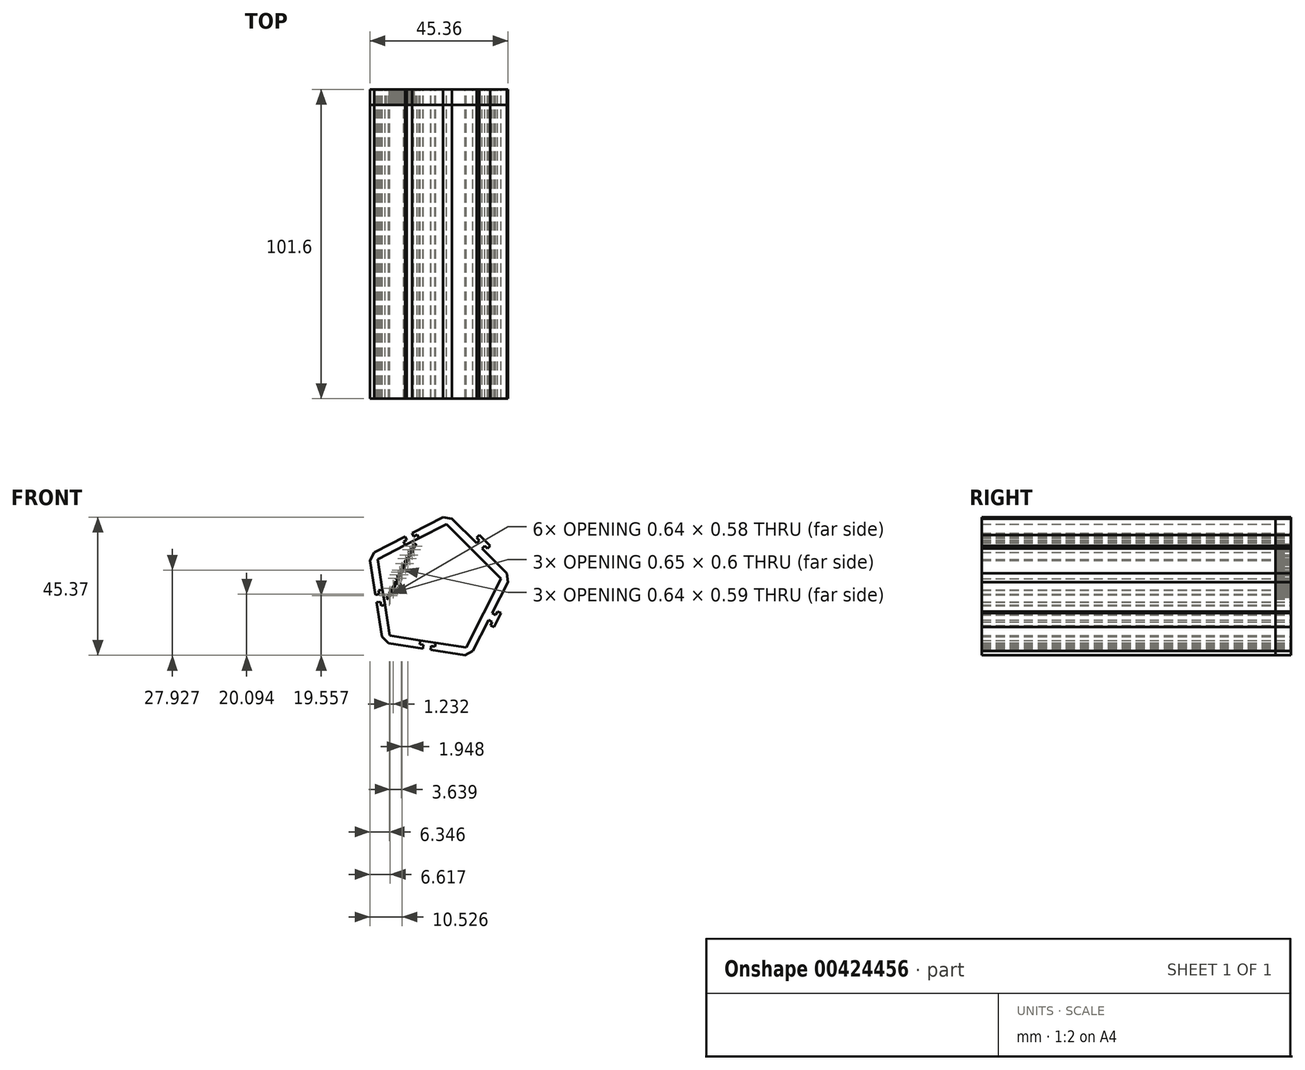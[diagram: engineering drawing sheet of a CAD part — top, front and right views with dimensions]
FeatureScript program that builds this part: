
annotation { "Feature Type Name" : "Feature", "Feature Type Description" : "" }
export const myFeature = defineFeature(function(context is Context, id is Id, definition is map)
    precondition{}
    {
        {
            var Q0;
            Q0=qCreatedBy(makeId("Front.planeOp"),FACE);
            var sketch = newSketch(context, id + "F0", { "sketchPlane" : qUnion([Q0])});
            skLineSegment(sketch, "E0", {"start": v(-27.51, 38.72) * mm, "end": v(-23.54, 13.64) * mm});
            skLineSegment(sketch, "E1", {"start": v(-23.54, 13.64) * mm, "end": v(1.55, 9.66) * mm});
            skLineSegment(sketch, "E2", {"start": v(1.55, 9.66) * mm, "end": v(13.08, 32.3) * mm});
            skLineSegment(sketch, "E3", {"start": v(13.08, 32.3) * mm, "end": v(-4.88, 50.26) * mm});
            skLineSegment(sketch, "E4", {"start": v(-4.88, 50.26) * mm, "end": v(-27.51, 38.72) * mm});
            skLineSegment(sketch, "E5", {"start": v(-27.51, 38.72) * mm, "end": v(-28.67, 40.99) * mm});
            skLineSegment(sketch, "E6", {"start": v(-4.88, 50.26) * mm, "end": v(-6.04, 52.52) * mm});
            skLineSegment(sketch, "E7", {"start": v(-28.67, 40.99) * mm, "end": v(-18.48, 46.18) * mm});
            skLineSegment(sketch, "E8", {"start": v(-6.04, 52.52) * mm, "end": v(-16.22, 47.33) * mm});
            skLineSegment(sketch, "E9", {"start": v(-18.48, 46.18) * mm, "end": v(-17.9, 45.04) * mm});
            skLineSegment(sketch, "E10", {"start": v(-17.9, 45.04) * mm, "end": v(-19.04, 44.47) * mm});
            skLineSegment(sketch, "E11", {"start": v(-19.04, 44.47) * mm, "end": v(-18.46, 43.34) * mm});
            skLineSegment(sketch, "E12", {"start": v(-16.22, 47.33) * mm, "end": v(-15.64, 46.2) * mm});
            skLineSegment(sketch, "E13", {"start": v(-15.64, 46.2) * mm, "end": v(-14.51, 46.77) * mm});
            skLineSegment(sketch, "E14", {"start": v(-14.51, 46.77) * mm, "end": v(-13.94, 45.64) * mm});
            skLineSegment(sketch, "E15", {"start": v(-4.88, 50.26) * mm, "end": v(-3.09, 52.05) * mm});
            skLineSegment(sketch, "E16", {"start": v(13.08, 32.3) * mm, "end": v(14.87, 34.1) * mm});
            skLineSegment(sketch, "E17", {"start": v(-3.09, 52.05) * mm, "end": v(5, 43.97) * mm});
            skLineSegment(sketch, "E18", {"start": v(14.87, 34.1) * mm, "end": v(6.8, 42.17) * mm});
            skLineSegment(sketch, "E19", {"start": v(5, 43.97) * mm, "end": v(5.9, 44.87) * mm});
            skLineSegment(sketch, "E20", {"start": v(6.8, 42.17) * mm, "end": v(7.69, 43.07) * mm});
            skLineSegment(sketch, "E21", {"start": v(5.9, 44.87) * mm, "end": v(5, 45.76) * mm});
            skLineSegment(sketch, "E22", {"start": v(5, 45.76) * mm, "end": v(5.9, 46.66) * mm});
            skLineSegment(sketch, "E23", {"start": v(5.9, 46.66) * mm, "end": v(9.49, 43.07) * mm});
            skLineSegment(sketch, "E24", {"start": v(9.49, 43.07) * mm, "end": v(8.59, 42.17) * mm});
            skLineSegment(sketch, "E25", {"start": v(7.69, 43.07) * mm, "end": v(8.59, 42.17) * mm});
            skLineSegment(sketch, "E26", {"start": v(-6.04, 52.52) * mm, "end": v(-3.09, 52.05) * mm});
            skLineSegment(sketch, "E27", {"start": v(13.08, 32.3) * mm, "end": v(15.34, 31.14) * mm});
            skLineSegment(sketch, "E28", {"start": v(15.34, 31.14) * mm, "end": v(10.15, 20.96) * mm});
            skLineSegment(sketch, "E29", {"start": v(1.55, 9.66) * mm, "end": v(3.8, 8.5) * mm});
            skLineSegment(sketch, "E30", {"start": v(3.8, 8.5) * mm, "end": v(9, 18.7) * mm});
            skLineSegment(sketch, "E31", {"start": v(14.87, 34.1) * mm, "end": v(15.34, 31.14) * mm});
            skLineSegment(sketch, "E32", {"start": v(-23.54, 13.64) * mm, "end": v(-23.94, 11.13) * mm});
            skLineSegment(sketch, "E33", {"start": v(-23.94, 11.13) * mm, "end": v(-12.65, 9.34) * mm});
            skLineSegment(sketch, "E34", {"start": v(-12.65, 9.34) * mm, "end": v(-12.45, 10.6) * mm});
            skLineSegment(sketch, "E35", {"start": v(-12.45, 10.6) * mm, "end": v(-13.7, 10.8) * mm});
            skLineSegment(sketch, "E36", {"start": v(-13.7, 10.8) * mm, "end": v(-13.5, 12.05) * mm});
            skLineSegment(sketch, "E37", {"start": v(1.55, 9.66) * mm, "end": v(1.15, 7.15) * mm});
            skLineSegment(sketch, "E38", {"start": v(1.15, 7.15) * mm, "end": v(-10.14, 8.94) * mm});
            skLineSegment(sketch, "E39", {"start": v(-10.14, 8.94) * mm, "end": v(-9.94, 10.2) * mm});
            skLineSegment(sketch, "E40", {"start": v(-9.94, 10.2) * mm, "end": v(-8.69, 10) * mm});
            skLineSegment(sketch, "E41", {"start": v(-8.69, 10) * mm, "end": v(-8.49, 11.25) * mm});
            skLineSegment(sketch, "E42", {"start": v(1.15, 7.15) * mm, "end": v(3.8, 8.5) * mm});
            skLineSegment(sketch, "E43", {"start": v(-27.51, 38.72) * mm, "end": v(-30.02, 38.33) * mm});
            skLineSegment(sketch, "E44", {"start": v(-30.02, 38.33) * mm, "end": v(-28.24, 27.04) * mm});
            skLineSegment(sketch, "E45", {"start": v(-28.24, 27.04) * mm, "end": v(-26.98, 27.24) * mm});
            skLineSegment(sketch, "E46", {"start": v(-26.98, 27.24) * mm, "end": v(-27.18, 28.5) * mm});
            skLineSegment(sketch, "E47", {"start": v(-27.18, 28.5) * mm, "end": v(-25.93, 28.69) * mm});
            skLineSegment(sketch, "E48", {"start": v(-28.67, 40.99) * mm, "end": v(-30.02, 38.33) * mm});
            skLineSegment(sketch, "E49", {"start": v(-23.54, 13.64) * mm, "end": v(-26.05, 13.24) * mm});
            skLineSegment(sketch, "E50", {"start": v(-26.05, 13.24) * mm, "end": v(-23.94, 11.13) * mm});
            skLineSegment(sketch, "E51", {"start": v(-26.05, 13.24) * mm, "end": v(-27.84, 24.53) * mm});
            skLineSegment(sketch, "E52", {"start": v(-27.84, 24.53) * mm, "end": v(-26.58, 24.73) * mm});
            skLineSegment(sketch, "E53", {"start": v(-26.58, 24.73) * mm, "end": v(-26.39, 23.47) * mm});
            skLineSegment(sketch, "E54", {"start": v(-26.39, 23.47) * mm, "end": v(-25.13, 23.67) * mm});
            skLineSegment(sketch, "E55", {"start": v(10.15, 20.96) * mm, "end": v(11.28, 20.38) * mm});
            skLineSegment(sketch, "E56", {"start": v(11.28, 20.38) * mm, "end": v(11.86, 21.51) * mm});
            skLineSegment(sketch, "E57", {"start": v(11.86, 21.51) * mm, "end": v(13, 20.96) * mm});
            skLineSegment(sketch, "E58", {"start": v(10.14, 18.14) * mm, "end": v(9.56, 17) * mm});
            skLineSegment(sketch, "E59", {"start": v(9.56, 17) * mm, "end": v(10.7, 16.43) * mm});
            skLineSegment(sketch, "E60", {"start": v(13, 20.96) * mm, "end": v(10.7, 16.43) * mm});
            skLineSegment(sketch, "E61", {"start": v(9, 18.7) * mm, "end": v(10.14, 18.14) * mm});
            skText(sketch, "E62", { "text": "Designed by Jefferson DeGrove Bishop", "fontName": "Arimo-Regular.ttf"});
            const initialGuessF0  = {"E62": [-0.02392, 0.02554, 0.44713, 0.89447, 0.00083]};
            skSetInitialGuess(sketch, initialGuessF0);
            skSolve(sketch);
        }
        {
            var Q0;
            {var subQ0=sQuery(id+"F0.wireOp",EDGE,"E5");Q0=makeQuery(id+"F0.imprint","IMPRINT",FACE,{"disambiguationData":[TD([[makeQuery(id+"F0.imprint","IMPRINT",EDGE,{"derivedFrom":subQ0}),-1.0]])]});}
            var Q1;
            {var subQ0=sQuery(id+"F0.wireOp",EDGE,"E6");Q1=makeQuery(id+"F0.imprint","IMPRINT",FACE,{"disambiguationData":[TD([[makeQuery(id+"F0.imprint","IMPRINT",EDGE,{"derivedFrom":subQ0}),1.0]])]});}
            var Q2;
            Q2=makeQuery(id+"F0.imprint","IMPRINT",FACE,{"disambiguationData":[TD([[makeQuery(id+"F0.imprint","IMPRINT",EDGE,{"derivedFrom":sQuery(id+"F0.wireOp",EDGE,"E6")}),-1.0]])]});
            var Q3;
            Q3=makeQuery(id+"F0.imprint","IMPRINT",FACE,{"disambiguationData":[TD([[makeQuery(id+"F0.imprint","IMPRINT",EDGE,{"derivedFrom":sQuery(id+"F0.wireOp",EDGE,"E3")}),-1.0]])]});
            var Q4;
            Q4=makeQuery(id+"F0.imprint","IMPRINT",FACE,{"disambiguationData":[TD([[makeQuery(id+"F0.imprint","IMPRINT",EDGE,{"derivedFrom":sQuery(id+"F0.wireOp",EDGE,"E16")}),-1.0]])]});
            var Q5;
            Q5=makeQuery(id+"F0.imprint","IMPRINT",FACE,{"disambiguationData":[TD([[makeQuery(id+"F0.imprint","IMPRINT",EDGE,{"derivedFrom":sQuery(id+"F0.wireOp",EDGE,"E2")}),-1.0]])]});
            var Q6;
            Q6=makeQuery(id+"F0.imprint","IMPRINT",FACE,{"disambiguationData":[TD([[makeQuery(id+"F0.imprint","IMPRINT",EDGE,{"derivedFrom":sQuery(id+"F0.wireOp",EDGE,"E5")}),1.0]])]});
            var Q7;
            {var subQ0=sQuery(id+"F0.wireOp",EDGE,"E43");Q7=makeQuery(id+"F0.imprint","IMPRINT",FACE,{"disambiguationData":[TD([[makeQuery(id+"F0.imprint","IMPRINT",EDGE,{"derivedFrom":subQ0}),1.0]])]});}
            var Q8;
            Q8=makeQuery(id+"F0.imprint","IMPRINT",FACE,{"disambiguationData":[TD([[makeQuery(id+"F0.imprint","IMPRINT",EDGE,{"derivedFrom":sQuery(id+"F0.wireOp",EDGE,"E32")}),-1.0]])]});
            var Q9;
            {var subQ0=sQuery(id+"F0.wireOp",EDGE,"E32");Q9=makeQuery(id+"F0.imprint","IMPRINT",FACE,{"disambiguationData":[TD([[makeQuery(id+"F0.imprint","IMPRINT",EDGE,{"derivedFrom":subQ0}),1.0]])]});}
            var Q10;
            {var subQ0=sQuery(id+"F0.wireOp",EDGE,"E49");Q10=makeQuery(id+"F0.imprint","IMPRINT",FACE,{"disambiguationData":[TD([[makeQuery(id+"F0.imprint","IMPRINT",EDGE,{"derivedFrom":subQ0}),-1.0]])]});}
            var Q11;
            Q11=makeQuery(id+"F0.imprint","IMPRINT",FACE,{"disambiguationData":[TD([[makeQuery(id+"F0.imprint","IMPRINT",EDGE,{"derivedFrom":sQuery(id+"F0.wireOp",EDGE,"E29")}),-1.0]])]});
            var Q12;
            {var subQ0=sQuery(id+"F0.wireOp",EDGE,"E37");Q12=makeQuery(id+"F0.imprint","IMPRINT",FACE,{"disambiguationData":[TD([[makeQuery(id+"F0.imprint","IMPRINT",EDGE,{"derivedFrom":subQ0}),-1.0]])]});}
            extrude(context, id + "F1", {"entities" : qUnion([Q0, Q1, Q2, Q3, Q4, Q5, Q6, Q7, Q8, Q9, Q10, Q11, Q12]), "depth" : 101.6 * mm});
        }
        {
            var Q0;
            Q0 = qSketchRegion(id + "F0", true);
            extrude(context, id + "F2", {"entities" : qUnion([Q0]), "depth" : 5.08 * mm});
        }
    });
